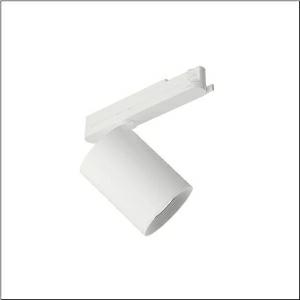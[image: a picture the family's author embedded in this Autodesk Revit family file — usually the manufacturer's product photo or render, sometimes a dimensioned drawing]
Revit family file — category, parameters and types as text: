
# Revit family: spot_21_51se14mbd5b
name_source: partatom
category: Lighting Fixtures
units: mm (PartAtom-declared; Revit-internal decimal feet)

## family parameters
Cut with Voids When Loaded = No
Host = Face
Light Source = No
Part Type = Normal
Room Calculation Point = No
Round Connector Dimension = Use Diameter
Shared = No

## types (1)
- --- (1 x LED, 5490 lm, 41.5 W, 4000K)
    Apparent Load = 42 VA
    CIE Flux Codes = 96 99 100 100 100
    Color Rendering = 90
    Color Temperature = 4000K
    Default Elevation = 1800 mm
    Description = Spot 21, directional spotlight, light control with lens, of PMMA, LED rated luminous flux: 5.270lm, light colour: 940, control gear: ECG Multilumen, with 3-phase adapter, mains connection: 220..240V, AC, 50/60Hz, of aluminium, traffic white (RAL 9016), length: 213mm, diameter: 105mm, protection rating (complete): IP20, insulation class (complete): insulation class I (protective earthing), certification: CE, impact resistance: IK02, permissible ambient temperature for indoor applications: -20..+40°C, packaging unit: 1 piece
    Height = 175 mm
    Lamp = 1 x LED
    Lamp Light Flux = 5490 lm
    Lamp Power = 41.5 W
    Lamp count = 1
    Length = 105 mm
    Luminous efficacy = 132 lm/W
    Manufacturer = Siteco
    ModVariant = No
    Model = 51SE14MBD5B
    Mounting Place = Ceiling
    Mounting Type = Pendant
    Number of Poles = 1
    OnlyDefault = Yes
    Power Factor = 1
    Product Name = Spot 21
    Product group = directional spotlight
    ProductGroupID = 904
    Protection Class = Protection class I
    Protection Degree = IP 20
    RLX_Detail_Level = 1
    RlxData = <blob elided: 17617 chars, md5=9d80cfca>
    Socket = socket
    Standby Power = 0 W
    System Light Flux = 5490 lm
    System Power = 42 W
    Type Comments = factory setting: luminous flux: 100 % | (ON | ON | ON | ON) | 1050 mA
    Type Image = l_1003976.jpg
    URL = http://relux.com
    VarID = @adj_052797
    Voltage = 0 V
    Weight = 0.00 kg
    Width = 0 mm  [stored 0 ft]

note: [stored X ft] marks values corroborated as IEEE doubles in the binary element streams (Revit-internal decimal feet)

## geometry (parser evidence)
native form markers: Blend x4, Sweep x12
no freeform markers — native parametric forms only
